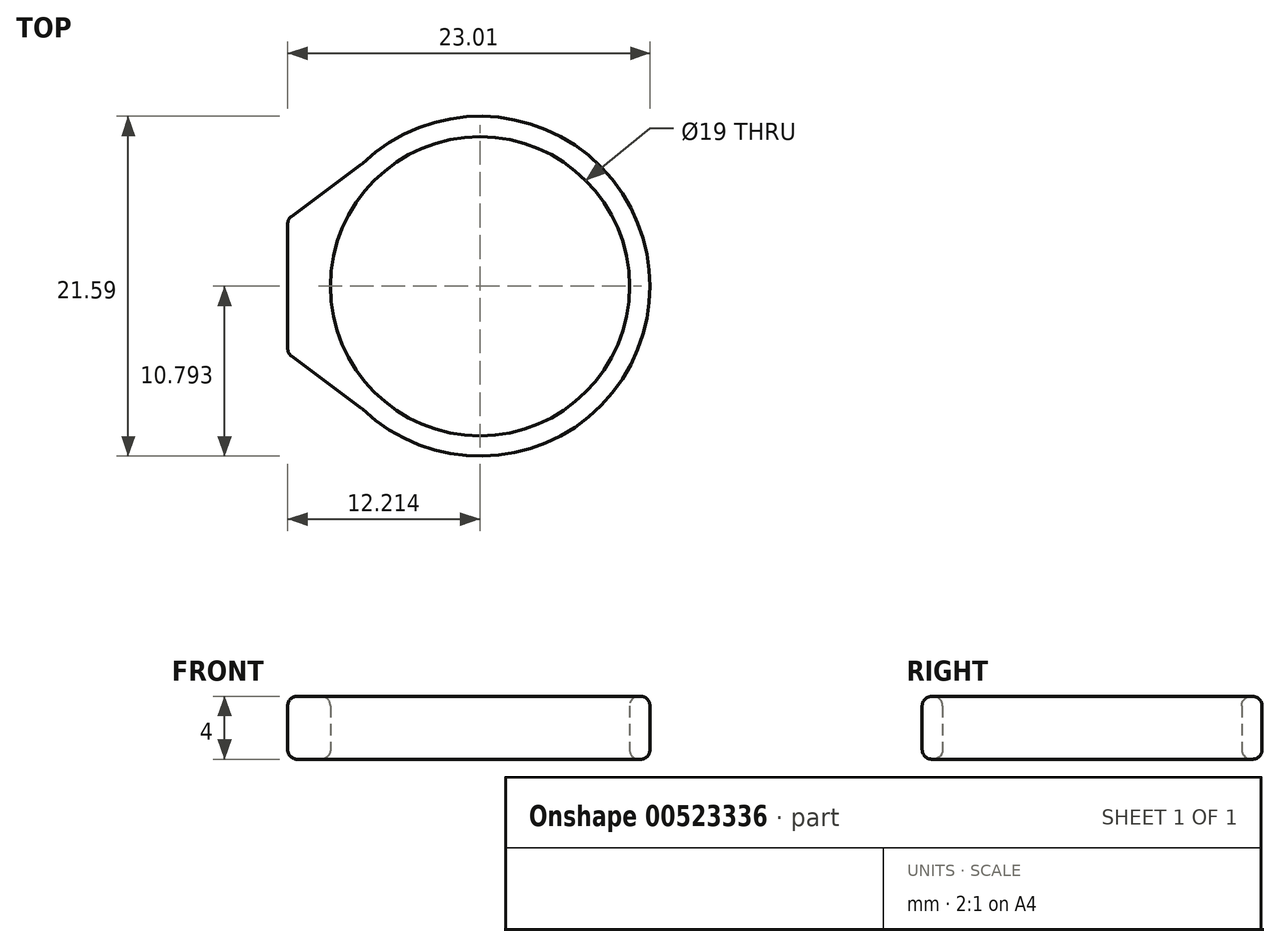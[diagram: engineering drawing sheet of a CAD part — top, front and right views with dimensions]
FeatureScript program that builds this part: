
annotation { "Feature Type Name" : "Feature", "Feature Type Description" : "" }
export const myFeature = defineFeature(function(context is Context, id is Id, definition is map)
    precondition{}
    {
        {
            var Q0;
            Q0=qCreatedBy(makeId("Top.planeOp"),FACE);
            var sketch = newSketch(context, id + "F0", { "sketchPlane" : qUnion([Q0])});
            skCircle(sketch, "E0", {"center": v(-12.9, -22.2) * mm, "radius": 9.5 * mm});
            skCircle(sketch, "E1", {"center": v(-12.9, -22.2) * mm, "radius": 10.8 * mm});
            skSolve(sketch);
        }
        {
            var Q0;
            Q0 = qSketchRegion(id + "F0", true);
            extrude(context, id + "F1", {"entities" : qUnion([Q0]), "depth" : 4 * mm, "offsetDistance" : 25 * mm});
        }
        {
            var Q0;
            Q0=makeQuery(id+"F1.opExtrude","CAP_FACE",FACE,{"disambiguationData":[OSD([sQuery(id+"F0.wireOp",EDGE,"E0"),sQuery(id+"F0.wireOp",EDGE,"E1")])],"isStart":false});
            var sketch = newSketch(context, id + "F2", { "sketchPlane" : qUnion([Q0])});
            skPoint(sketch, "E2", {"position": v(-22.82, -17.94) * mm});
            skPoint(sketch, "E3", {"position": v(-22.82, -26.46) * mm});
            skLineSegment(sketch, "E4.bottom", {"start": v(-22.82, -17.94) * mm, "end": v(-25.12, -17.94) * mm});
            skLineSegment(sketch, "E4.top", {"start": v(-22.82, -26.46) * mm, "end": v(-25.12, -26.46) * mm});
            skLineSegment(sketch, "E4.left", {"start": v(-22.82, -17.94) * mm, "end": v(-22.82, -26.46) * mm});
            skLineSegment(sketch, "E4.right", {"start": v(-25.12, -17.94) * mm, "end": v(-25.12, -26.46) * mm});
            skPoint(sketch, "E5", {"position": v(-18.2, -12.79) * mm});
            skPoint(sketch, "E6", {"position": v(-18.2, -31.6) * mm});
            skLineSegment(sketch, "E7", {"start": v(-18.2, -31.6) * mm, "end": v(-22.82, -26.46) * mm});
            skLineSegment(sketch, "E8", {"start": v(-18.2, -31.6) * mm, "end": v(-25.12, -26.46) * mm});
            skLineSegment(sketch, "E9", {"start": v(-18.2, -12.79) * mm, "end": v(-22.82, -17.94) * mm});
            skLineSegment(sketch, "E10", {"start": v(-18.2, -12.79) * mm, "end": v(-25.12, -17.94) * mm});
            skSolve(sketch);
        }
        {
            var Q0;
            Q0 = qSketchRegion(id + "F2", true);
            extrude(context, id + "F3", {"entities" : qUnion([Q0]), "operationType" : NewBodyOperationType.ADD, "oppositeDirection" : true, "depth" : 4 * mm, "offsetDistance" : 25 * mm});
        }
        {
            var Q0;
            Q0=makeQuery(id+"F1.opExtrude","CAP_EDGE",EDGE,{"disambiguationData":[OSD([sQuery(id+"F0.wireOp",EDGE,"E1")])],"isStart":false});
            var Q1;
            Q1=makeQuery(id+"F1.opExtrude","CAP_EDGE",EDGE,{"disambiguationData":[OSD([sQuery(id+"F0.wireOp",EDGE,"E1")])],"isStart":true});
            var Q2;
            Q2=makeQuery(id+"F3.opExtrude","CAP_EDGE",EDGE,{"disambiguationData":[OSD([sQuery(id+"F2.wireOp",EDGE,"E8")])],"isStart":false});
            var Q3;
            Q3=makeQuery(id+"F3.opExtrude","CAP_EDGE",EDGE,{"disambiguationData":[OSD([sQuery(id+"F2.wireOp",EDGE,"E4.right")])],"isStart":true});
            var Q4;
            Q4=makeQuery(id+"F3.opExtrude","CAP_EDGE",EDGE,{"disambiguationData":[OSD([sQuery(id+"F2.wireOp",EDGE,"E10")])],"isStart":true});
            var Q5;
            Q5=makeQuery(id+"F3.opExtrude","CAP_EDGE",EDGE,{"disambiguationData":[OSD([sQuery(id+"F2.wireOp",EDGE,"E4.right")])],"isStart":false});
            var Q6;
            Q6=makeQuery(id+"F3.opExtrude","CAP_EDGE",EDGE,{"disambiguationData":[OSD([sQuery(id+"F2.wireOp",EDGE,"E10")])],"isStart":false});
            var Q7;
            Q7=makeQuery(id+"F1.opExtrude","CAP_EDGE",EDGE,{"disambiguationData":[OSD([sQuery(id+"F0.wireOp",EDGE,"E0")])],"isStart":false});
            var Q8;
            Q8=makeQuery(id+"F1.opExtrude","CAP_EDGE",EDGE,{"disambiguationData":[OSD([sQuery(id+"F0.wireOp",EDGE,"E0")])],"isStart":true});
            var Q9;
            Q9=makeQuery(id+"F3.opExtrude","SWEPT_EDGE",EDGE,{"disambiguationData":[OSD([sQuery(id+"F2.wireOp",EDGE,"E4.top"),sQuery(id+"F2.wireOp",EDGE,"E4.right"),sQuery(id+"F2.wireOp",EDGE,"E8")])]});
            var Q10;
            Q10=makeQuery(id+"F3.opExtrude","SWEPT_EDGE",EDGE,{"disambiguationData":[OSD([sQuery(id+"F2.wireOp",EDGE,"E4.bottom"),sQuery(id+"F2.wireOp",EDGE,"E4.right"),sQuery(id+"F2.wireOp",EDGE,"E10")])]});
            var Q11;
            Q11=makeQuery(id+"F3.boolean.opBoolean","INTERSECT",EDGE,{"derivedFrom":[makeQuery(id+"F1.opExtrude","SWEPT_FACE",FACE,{"disambiguationData":[OSD([sQuery(id+"F0.wireOp",EDGE,"E1")])]}),makeQuery(id+"F3.opExtrude","SWEPT_FACE",FACE,{"disambiguationData":[OSD([sQuery(id+"F2.wireOp",EDGE,"E10")])]})]});
            var Q12;
            Q12=makeQuery(id+"F3.boolean.opBoolean","INTERSECT",EDGE,{"derivedFrom":[makeQuery(id+"F1.opExtrude","SWEPT_FACE",FACE,{"disambiguationData":[OSD([sQuery(id+"F0.wireOp",EDGE,"E1")])]}),makeQuery(id+"F3.opExtrude","SWEPT_FACE",FACE,{"disambiguationData":[OSD([sQuery(id+"F2.wireOp",EDGE,"E8")])]})]});
            var Q13;
            Q13=makeQuery(id+"F3.opExtrude","CAP_EDGE",EDGE,{"disambiguationData":[OSD([sQuery(id+"F2.wireOp",EDGE,"E8")])],"isStart":true});
            fillet(context, id + "F4", {"entities" : qUnion([Q0, Q1, Q2, Q3, Q4, Q5, Q6, Q7, Q8, Q9, Q10, Q11, Q12, Q13]), "radius" : .6 * mm, "tangentPropagation" : true, "allowEdgeOverflow" : false});
        }
    });
